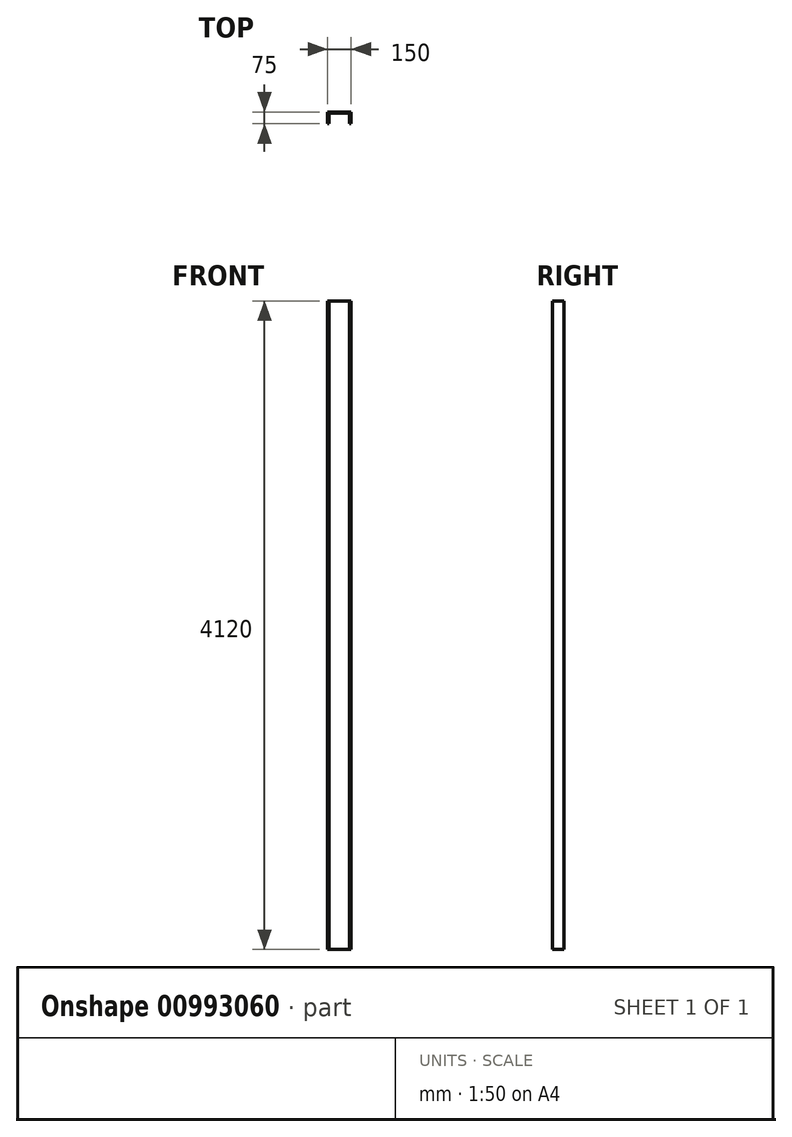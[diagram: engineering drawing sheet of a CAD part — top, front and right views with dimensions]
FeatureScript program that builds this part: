
annotation { "Feature Type Name" : "Feature", "Feature Type Description" : "" }
export const myFeature = defineFeature(function(context is Context, id is Id, definition is map)
    precondition{}
    {
        {
            var Q0;
            Q0=qCreatedBy(makeId("Top.planeOp"),FACE);
            var sketch = newSketch(context, id + "F0", { "sketchPlane" : qUnion([Q0])});
            skLineSegment(sketch, "E0", {"start": v(0, 0) * mm, "end": v(0, 75) * mm});
            skLineSegment(sketch, "E1", {"start": v(0, 75) * mm, "end": v(150, 75) * mm});
            skLineSegment(sketch, "E2", {"start": v(150, 75) * mm, "end": v(150, 0) * mm});
            skLineSegment(sketch, "E3", {"start": v(150, 0) * mm, "end": v(140, 0) * mm});
            skLineSegment(sketch, "E4", {"start": v(140, 0) * mm, "end": v(140, 69.5) * mm});
            skLineSegment(sketch, "E5", {"start": v(140, 69.5) * mm, "end": v(10, 69.5) * mm});
            skLineSegment(sketch, "E6", {"start": v(10, 69.5) * mm, "end": v(10, 0) * mm});
            skLineSegment(sketch, "E7", {"start": v(10, 0) * mm, "end": v(0, 0) * mm});
            skSolve(sketch);
        }
        {
            var Q0;
            Q0=makeQuery(id+"F0.imprint","IMPRINT",FACE,{"disambiguationData":[TD([[makeQuery(id+"F0.imprint","IMPRINT",EDGE,{"derivedFrom":sQuery(id+"F0.wireOp",EDGE,"E0")}),-1.0]])]});
            extrude(context, id + "F1", {"entities" : qUnion([Q0]), "depth" : 4120 * mm, "offsetDistance" : 25 * mm});
        }
    });
